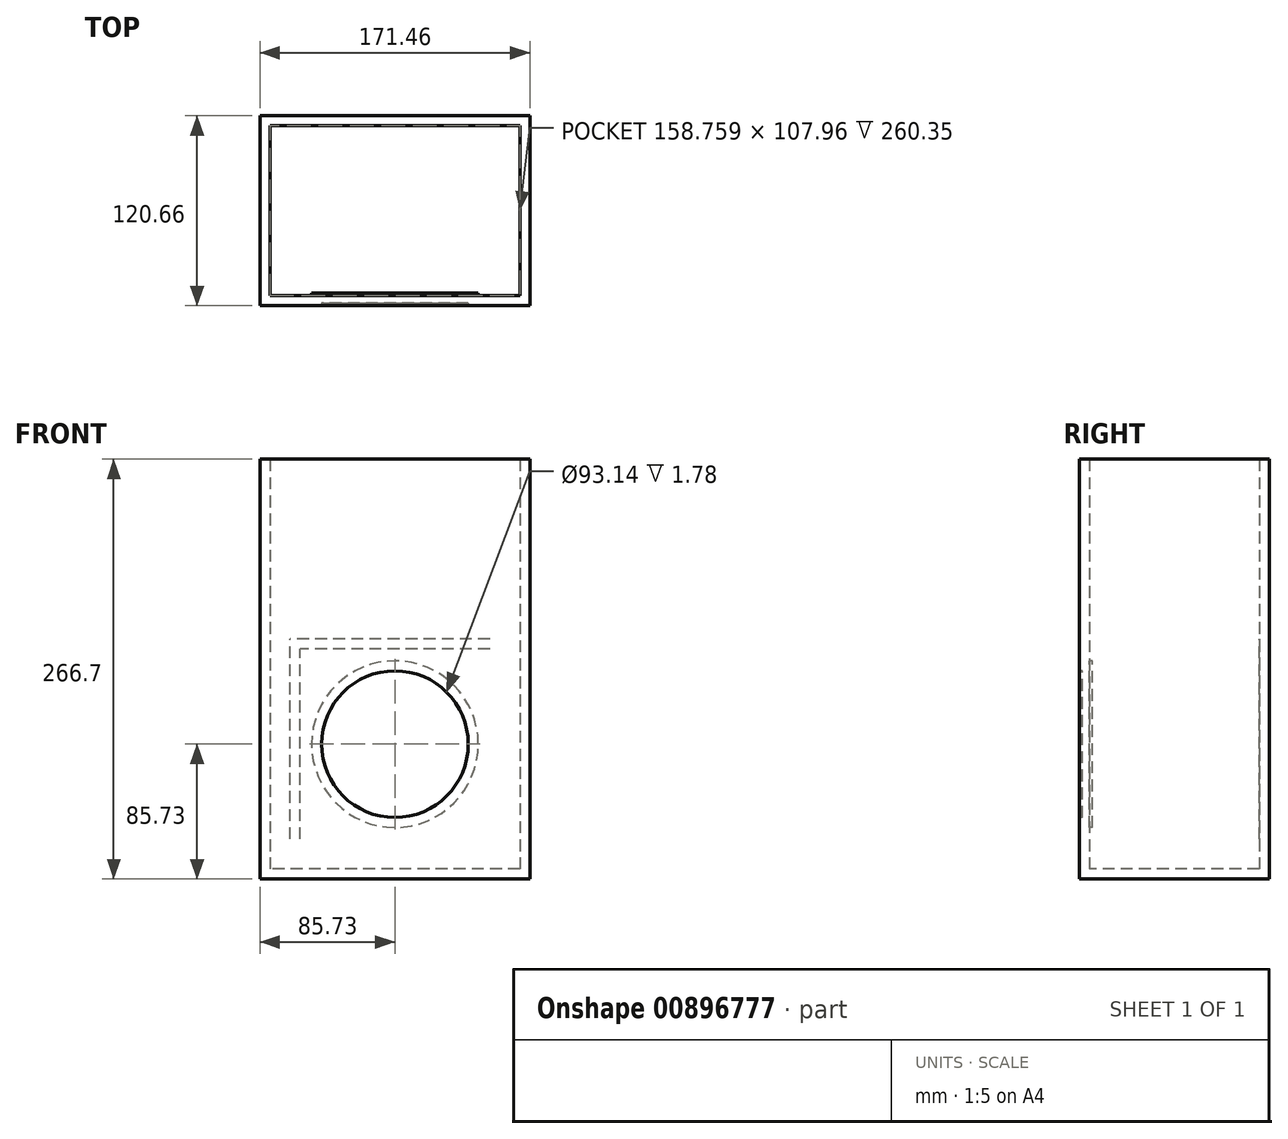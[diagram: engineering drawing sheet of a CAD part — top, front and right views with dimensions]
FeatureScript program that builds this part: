
annotation { "Feature Type Name" : "Feature", "Feature Type Description" : "" }
export const myFeature = defineFeature(function(context is Context, id is Id, definition is map)
    precondition{}
    {
        {
            var Q0;
            Q0=qCreatedBy(makeId("Top.planeOp"),FACE);
            var sketch = newSketch(context, id + "F0", { "sketchPlane" : qUnion([Q0])});
            skLineSegment(sketch, "E0.bottom", {"start": v(60.33, -60.33) * mm, "end": v(-60.32, -60.33) * mm});
            skLineSegment(sketch, "E0.top", {"start": v(60.32, 60.33) * mm, "end": v(-60.33, 60.32) * mm});
            skLineSegment(sketch, "E0.left", {"start": v(60.33, -60.33) * mm, "end": v(60.32, 60.33) * mm});
            skLineSegment(sketch, "E0.right", {"start": v(-60.32, -60.33) * mm, "end": v(-60.33, 60.32) * mm});
            skPoint(sketch, "E0.middle", {"position": v(0, 0) * mm});
            skSolve(sketch);
        }
        {
            var Q0;
            Q0=makeQuery(id+"F0.imprint","IMPRINT",FACE,{"disambiguationData":[TD([[makeQuery(id+"F0.imprint","IMPRINT",EDGE,{"derivedFrom":sQuery(id+"F0.wireOp",EDGE,"E0.bottom")}),-1.0]])]});
            extrude(context, id + "F1", {"entities" : qUnion([Q0]), "depth" : 120.65 * mm, "offsetDistance" : 25.4 * mm});
        }
        {
            var Q0;
            Q0=makeQuery(id+"F1.opExtrude","SWEPT_FACE",FACE,{"disambiguationData":[OSD([sQuery(id+"F0.wireOp",EDGE,"E0.bottom")])]});
            var sketch = newSketch(context, id + "F2", { "sketchPlane" : qUnion([Q0])});
            skCircle(sketch, "E1", {"center": v(0, 60.33) * mm, "radius": 46.57 * mm});
            skPoint(sketch, "E1.centerSnap0", {"position": v(60.33, 60.33) * mm});
            skSolve(sketch);
        }
        {
            var Q0;
            Q0=makeQuery(id+"F2.imprint","IMPRINT",FACE,{"disambiguationData":[TD([[makeQuery(id+"F2.imprint","IMPRINT",EDGE,{"derivedFrom":sQuery(id+"F2.wireOp",EDGE,"E1")}),1.0]])]});
            extrude(context, id + "F3", {"entities" : qUnion([Q0]), "operationType" : NewBodyOperationType.REMOVE, "oppositeDirection" : true, "depth" : 1.78 * mm, "offsetDistance" : 25.4 * mm});
        }
        {
            var Q0;
            Q0=makeQuery(id+"F1.opExtrude","SWEPT_BODY",BODY,{"disambiguationData":[OSD([sQuery(id+"F0.wireOp",EDGE,"E0.bottom"),sQuery(id+"F0.wireOp",EDGE,"E0.top"),sQuery(id+"F0.wireOp",EDGE,"E0.left"),sQuery(id+"F0.wireOp",EDGE,"E0.right")])]});
            var Q1;
            Q1=makeQuery(id+"F1.opExtrude","CAP_EDGE",EDGE,{"disambiguationData":[OSD([sQuery(id+"F0.wireOp",EDGE,"E0.bottom")])],"isStart":false});
            transform(context, id + "F4", {"entities" : qUnion([Q0]), "transformType" : TransformType.TRANSLATION_3D, "dx" : 0 * mm, "dy" : 0 * mm, "dz" : 25.4 * mm, "makeCopy" : false});
        }
        {
            var Q0;
            Q0=qCreatedBy(makeId("Top.planeOp"),FACE);
            var sketch = newSketch(context, id + "F5", { "sketchPlane" : qUnion([Q0])});
            skLineSegment(sketch, "E2.bottom", {"start": v(85.72, 60.33) * mm, "end": v(-85.73, 60.33) * mm});
            skLineSegment(sketch, "E2.top", {"start": v(85.73, -60.33) * mm, "end": v(-85.72, -60.33) * mm});
            skLineSegment(sketch, "E2.left", {"start": v(85.72, 60.33) * mm, "end": v(85.73, -60.33) * mm});
            skLineSegment(sketch, "E2.right", {"start": v(-85.73, 60.33) * mm, "end": v(-85.72, -60.33) * mm});
            skPoint(sketch, "E2.middle", {"position": v(0, 0) * mm});
            skSolve(sketch);
        }
        {
            var Q0;
            Q0=makeQuery(id+"F5.imprint","IMPRINT",FACE,{"disambiguationData":[TD([[makeQuery(id+"F5.imprint","IMPRINT",EDGE,{"derivedFrom":sQuery(id+"F5.wireOp",EDGE,"E2.bottom")}),1.0]])]});
            extrude(context, id + "F6", {"entities" : qUnion([Q0]), "depth" : 25.4 * mm, "offsetDistance" : 25.4 * mm});
        }
        {
            var Q0;
            Q0=makeQuery(id+"F6.opExtrude","CAP_FACE",FACE,{"disambiguationData":[OSD([sQuery(id+"F5.wireOp",EDGE,"E2.bottom"),sQuery(id+"F5.wireOp",EDGE,"E2.top"),sQuery(id+"F5.wireOp",EDGE,"E2.left"),sQuery(id+"F5.wireOp",EDGE,"E2.right")])],"isStart":false});
            var sketch = newSketch(context, id + "F7", { "sketchPlane" : qUnion([Q0])});
            skLineSegment(sketch, "E3", {"start": v(-60.32, 60.33) * mm, "end": v(-60.32, -60.33) * mm});
            skLineSegment(sketch, "E4", {"start": v(60.32, 60.33) * mm, "end": v(60.33, -60.33) * mm});
            skSolve(sketch);
        }
        {
            var Q0;
            {var subQ0=sQuery(id+"F7.wireOp",EDGE,"E3");Q0=makeQuery(id+"F7.imprint","IMPRINT",FACE,{"disambiguationData":[TD([[makeQuery(id+"F7.imprint","IMPRINT",EDGE,{"derivedFrom":subQ0}),-1.0]])]});}
            var Q1;
            {var subQ0=sQuery(id+"F7.wireOp",EDGE,"E4");Q1=makeQuery(id+"F7.imprint","IMPRINT",FACE,{"disambiguationData":[TD([[makeQuery(id+"F7.imprint","IMPRINT",EDGE,{"derivedFrom":subQ0}),1.0]])]});}
            extrude(context, id + "F8", {"entities" : qUnion([Q0, Q1]), "operationType" : NewBodyOperationType.ADD, "depth" : 120.65 * mm, "offsetDistance" : 25.4 * mm});
        }
        {
            var Q0;
            Q0=makeQuery(id+"F8.opExtrude","CAP_FACE",FACE,{"disambiguationData":[OSD([sQuery(id+"F5.wireOp",EDGE,"E2.bottom"),sQuery(id+"F5.wireOp",EDGE,"E2.top"),sQuery(id+"F5.wireOp",EDGE,"E2.right"),sQuery(id+"F7.wireOp",EDGE,"E3")])],"isStart":false});
            var Q1;
            Q1=makeQuery(id+"F8.opExtrude","CAP_FACE",FACE,{"disambiguationData":[OSD([sQuery(id+"F5.wireOp",EDGE,"E2.bottom"),sQuery(id+"F5.wireOp",EDGE,"E2.top"),sQuery(id+"F5.wireOp",EDGE,"E2.left"),sQuery(id+"F7.wireOp",EDGE,"E4")])],"isStart":false});
            extrude(context, id + "F9", {"entities" : qUnion([Q0, Q1]), "operationType" : NewBodyOperationType.ADD, "depth" : 120.65 * mm, "offsetDistance" : 25.4 * mm});
        }
        {
            var Q0;
            {var subQ0=sQuery(id+"F7.wireOp",EDGE,"E3");Q0=makeQuery(id+"F9.boolean.opBoolean","MERGE",FACE,{"derivedFrom":[makeQuery(id+"F8.opExtrude","SWEPT_FACE",FACE,{"disambiguationData":[OSD([subQ0])]}),makeQuery(id+"F9.opExtrude","SWEPT_FACE",FACE,{"disambiguationData":[OSD([subQ0])]})]});}
            var sketch = newSketch(context, id + "F10", { "sketchPlane" : qUnion([Q0])});
            skLineSegment(sketch, "E5", {"start": v(-60.33, 146.05) * mm, "end": v(60.33, 146.05) * mm});
            skSolve(sketch);
        }
        {
            var Q0;
            {var subQ0=sQuery(id+"F10.wireOp",EDGE,"E5");Q0=makeQuery(id+"F10.imprint","IMPRINT",FACE,{"disambiguationData":[TD([[makeQuery(id+"F10.imprint","IMPRINT",EDGE,{"derivedFrom":subQ0}),1.0]])]});}
            extrude(context, id + "F11", {"entities" : qUnion([Q0]), "operationType" : NewBodyOperationType.ADD, "depth" : 120.65 * mm, "offsetDistance" : 25.4 * mm});
        }
        {
            var Q0;
            {var subQ0=sQuery(id+"F7.wireOp",EDGE,"E3");var subQ1=sQuery(id+"F5.wireOp",EDGE,"E2.top");var subQ2=sQuery(id+"F5.wireOp",EDGE,"E2.bottom");Q0=makeQuery(id+"F11.boolean.opBoolean","MERGE",FACE,{"derivedFrom":[makeQuery(id+"F9.opExtrude","CAP_FACE",FACE,{"disambiguationData":[OSD([subQ2,subQ1,sQuery(id+"F5.wireOp",EDGE,"E2.right"),subQ0])],"isStart":false}),makeQuery(id+"F9.opExtrude","CAP_FACE",FACE,{"disambiguationData":[OSD([subQ2,subQ1,sQuery(id+"F5.wireOp",EDGE,"E2.left"),sQuery(id+"F7.wireOp",EDGE,"E4")])],"isStart":false}),makeQuery(id+"F11.opExtrude","SWEPT_FACE",FACE,{"disambiguationData":[OSD([subQ0])]})]});}
            shell(context, id + "F12", {"entities" : qUnion([Q0]), "thickness" : 6.35 * mm});
        }
    });
